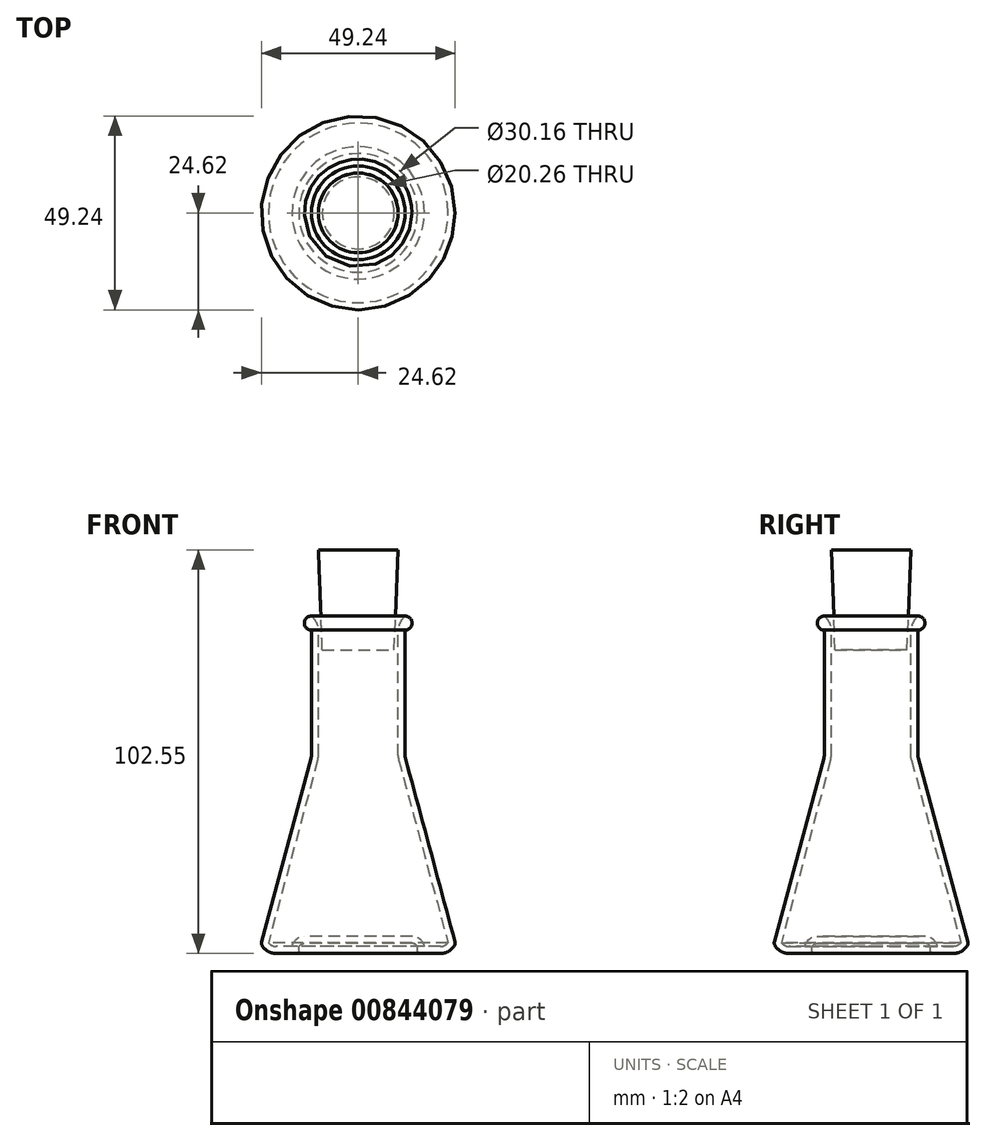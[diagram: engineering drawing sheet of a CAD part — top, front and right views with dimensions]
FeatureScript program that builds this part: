
annotation { "Feature Type Name" : "Feature", "Feature Type Description" : "" }
export const myFeature = defineFeature(function(context is Context, id is Id, definition is map)
    precondition{}
    {
        {
            var Q0;
            Q0=qCreatedBy(makeId("Front.planeOp"),FACE);
            var sketch = newSketch(context, id + "F0", { "sketchPlane" : qUnion([Q0])});
            skLineSegment(sketch, "E0", {"start": v(0, 0) * mm, "end": v(13.81, 0) * mm});
            skLineSegment(sketch, "E1", {"start": v(15.08, -1.27) * mm, "end": v(15.08, -2.03) * mm});
            skLineSegment(sketch, "E2", {"start": v(15.59, -2.54) * mm, "end": v(20.86, -2.54) * mm});
            skArc(sketch, "E3", {"start": v(20.86, -2.54) * mm, "mid": v(22.92, -2) * mm, "end": v(24.44, -0.52) * mm});
            skLineSegment(sketch, "E4", {"start": v(24.58, 0.47) * mm, "end": v(12, 47.08) * mm});
            skLineSegment(sketch, "E5", {"start": v(11.9, 47.75) * mm, "end": v(11.9, 79.63) * mm});
            skArc(sketch, "E6", {"start": v(11.9, 79.63) * mm, "mid": v(13.68, 81.4) * mm, "end": v(11.9, 83.19) * mm});
            skLineSegment(sketch, "E7", {"start": v(11.9, 83.19) * mm, "end": v(0, 83.19) * mm});
            skLineSegment(sketch, "E8", {"start": v(0, 83.19) * mm, "end": v(0, 0) * mm});
            skPoint(sketch, "E9.visualSharp", {"position": v(15.08, -2.54) * mm});
            skArc(sketch, "E9.filletArc", {"start": v(15.08, -2.03) * mm, "mid": v(15.23, -2.4) * mm, "end": v(15.59, -2.54) * mm});
            skPoint(sketch, "E10.visualSharp", {"position": v(15.08, 0) * mm});
            skArc(sketch, "E10.filletArc", {"start": v(15.08, -1.27) * mm, "mid": v(14.7, -0.37) * mm, "end": v(13.81, 0) * mm});
            skPoint(sketch, "E11.visualSharp", {"position": v(24.7, 0) * mm});
            skArc(sketch, "E11.filletArc", {"start": v(24.44, -0.52) * mm, "mid": v(24.61, -0.04) * mm, "end": v(24.58, 0.47) * mm});
            skPoint(sketch, "E12.visualSharp", {"position": v(11.9, 47.4) * mm});
            skArc(sketch, "E12.filletArc", {"start": v(11.9, 47.75) * mm, "mid": v(11.93, 47.41) * mm, "end": v(12, 47.08) * mm});
            skSolve(sketch);
        }
        {
            var Q0;
            Q0=makeQuery(id+"F0.imprint","IMPRINT",FACE,{"disambiguationData":[TD([[makeQuery(id+"F0.imprint","IMPRINT",EDGE,{"derivedFrom":sQuery(id+"F0.wireOp",EDGE,"E0")}),1.0]])]});
            var Q1;
            Q1=sQuery(id+"F0.wireOp",EDGE,"E8");
            revolve(context, id + "F1", {"surfaceOperationType" : NewSurfaceOperationType.NEW, "entities" : qUnion([Q0]), "axis" : qUnion([Q1]), "revolveType" : RevolveType.FULL});
        }
        {
            var Q0;
            Q0=makeQuery(id+"F1.opRevolve","SWEPT_FACE",FACE,{"disambiguationData":[OSD([sQuery(id+"F0.wireOp",EDGE,"E7")])]});
            shell(context, id + "F2", {"entities" : qUnion([Q0]), "thickness" : 1.78 * mm});
        }
        {
            var Q0;
            Q0=makeQuery(id+"F2.opShell","OFFSET_EDGE",EDGE,{"disambiguationData":[OSD([sQuery(id+"F0.wireOp",EDGE,"E5"),sQuery(id+"F0.wireOp",EDGE,"E6"),sQuery(id+"F0.wireOp",EDGE,"E7")])]});
            fillet(context, id + "F3", {"entities" : qUnion([Q0]), "radius" : 5.08 * mm, "tangentPropagation" : true, "allowEdgeOverflow" : false});
        }
        {
            var Q0;
            Q0=qCreatedBy(makeId("Front.planeOp"),FACE);
            var sketch = newSketch(context, id + "F4", { "sketchPlane" : qUnion([Q0])});
            skLineSegment(sketch, "E13", {"start": v(0, 100.01) * mm, "end": v(-10.12, 100.01) * mm});
            skLineSegment(sketch, "E14", {"start": v(-10.12, 100.01) * mm, "end": v(-9.14, 74.61) * mm});
            skLineSegment(sketch, "E15", {"start": v(-9.14, 74.61) * mm, "end": v(0, 74.61) * mm});
            skLineSegment(sketch, "E16", {"start": v(0, 74.61) * mm, "end": v(0, 100.01) * mm});
            skSolve(sketch);
        }
        {
            var Q0;
            Q0=makeQuery(id+"F4.imprint","IMPRINT",FACE,{"disambiguationData":[TD([[makeQuery(id+"F4.imprint","IMPRINT",EDGE,{"derivedFrom":sQuery(id+"F4.wireOp",EDGE,"E13")}),1.0]])]});
            var Q1;
            Q1=sQuery(id+"F4.wireOp",EDGE,"E16");
            revolve(context, id + "F5", {"surfaceOperationType" : NewSurfaceOperationType.NEW, "entities" : qUnion([Q0]), "axis" : qUnion([Q1]), "revolveType" : RevolveType.FULL});
        }
    });
